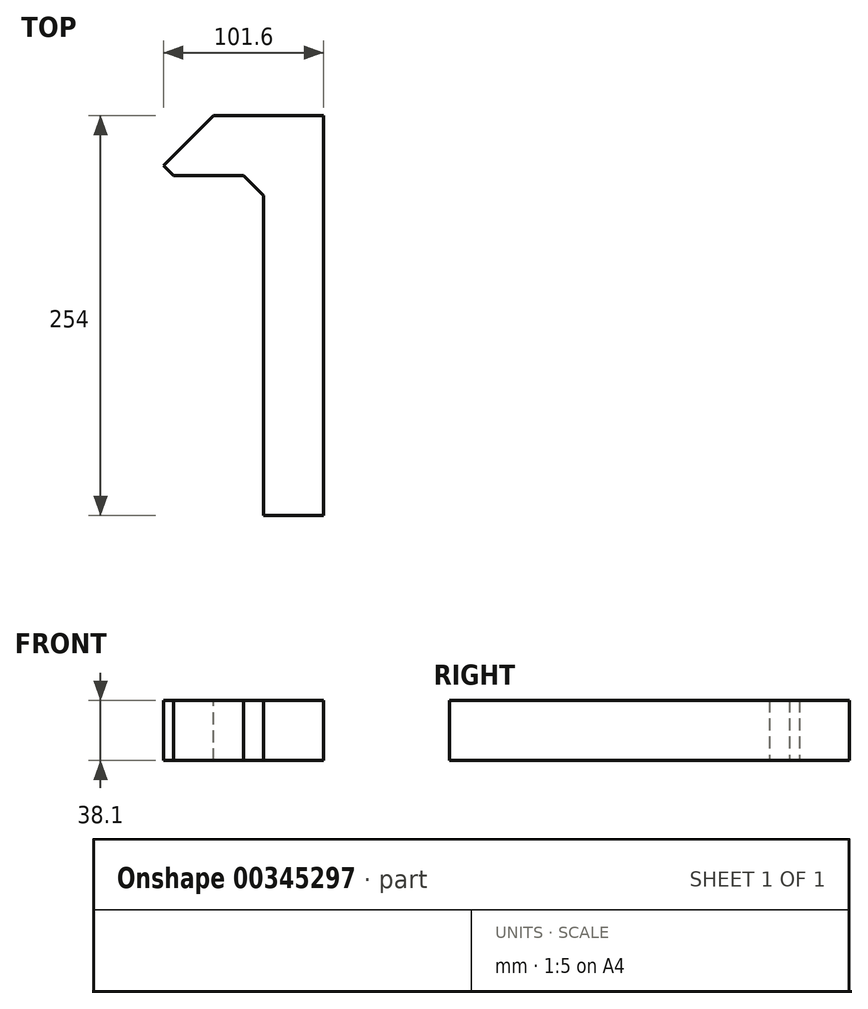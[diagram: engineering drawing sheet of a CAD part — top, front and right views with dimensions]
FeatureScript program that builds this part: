
annotation { "Feature Type Name" : "Feature", "Feature Type Description" : "" }
export const myFeature = defineFeature(function(context is Context, id is Id, definition is map)
    precondition{}
    {
        {
            var Q0;
            Q0=qCreatedBy(makeId("Top.planeOp"),FACE);
            var sketch = newSketch(context, id + "F0", { "sketchPlane" : qUnion([Q0])});
            skLineSegment(sketch, "E0.bottom", {"start": v(19.05, -127) * mm, "end": v(-19.05, -127) * mm});
            skLineSegment(sketch, "E0.top", {"start": v(19.05, 127) * mm, "end": v(-19.05, 127) * mm});
            skLineSegment(sketch, "E0.left", {"start": v(19.05, -127) * mm, "end": v(19.05, 127) * mm});
            skLineSegment(sketch, "E0.right", {"start": v(-19.05, -127) * mm, "end": v(-19.05, 127) * mm});
            skPoint(sketch, "E0.middle", {"position": v(0, 0) * mm});
            skLineSegment(sketch, "E1.bottom", {"start": v(19.05, 127) * mm, "end": v(-82.55, 127) * mm});
            skLineSegment(sketch, "E1.top", {"start": v(19.05, 88.9) * mm, "end": v(-82.55, 88.9) * mm});
            skLineSegment(sketch, "E1.left", {"start": v(19.05, 127) * mm, "end": v(19.05, 88.9) * mm});
            skLineSegment(sketch, "E1.right", {"start": v(-82.55, 127) * mm, "end": v(-82.55, 88.9) * mm});
            skSolve(sketch);
        }
        {
            var Q0;
            Q0 = qSketchRegion(id + "F0", true);
            extrude(context, id + "F1", {"entities" : qUnion([Q0]), "depth" : 38.1 * mm});
        }
        {
            var Q0;
            Q0=makeQuery(id+"F1.opExtrude","SWEPT_EDGE",EDGE,{"disambiguationData":[OSD([sQuery(id+"F0.wireOp",EDGE,"E0.right"),sQuery(id+"F0.wireOp",EDGE,"E1.top")])]});
            chamfer(context, id + "F2", {"entities" : qUnion([Q0]), "width" : 12.7 * mm, "tangentPropagation" : true});
        }
        {
            var Q0;
            Q0=makeQuery(id+"F1.opExtrude","SWEPT_EDGE",EDGE,{"disambiguationData":[OSD([sQuery(id+"F0.wireOp",EDGE,"E1.bottom"),sQuery(id+"F0.wireOp",EDGE,"E1.left")])]});
            chamfer(context, id + "F3", {"entities" : qUnion([Q0]), "width" : 31.75 * mm, "tangentPropagation" : true});
        }
        {
            var Q0;
            Q0=makeQuery(id+"F1.opExtrude","SWEPT_EDGE",EDGE,{"disambiguationData":[OSD([sQuery(id+"F0.wireOp",EDGE,"E1.top"),sQuery(id+"F0.wireOp",EDGE,"E1.right")])]});
            var Q1;
            Q1=makeQuery(id+"F1.opExtrude","SWEPT_EDGE",EDGE,{"disambiguationData":[OSD([sQuery(id+"F0.wireOp",EDGE,"E1.bottom"),sQuery(id+"F0.wireOp",EDGE,"E1.right")])]});
            chamfer(context, id + "F4", {"entities" : qUnion([Q0, Q1]), "width" : 6.35 * mm, "tangentPropagation" : true});
        }
    });
